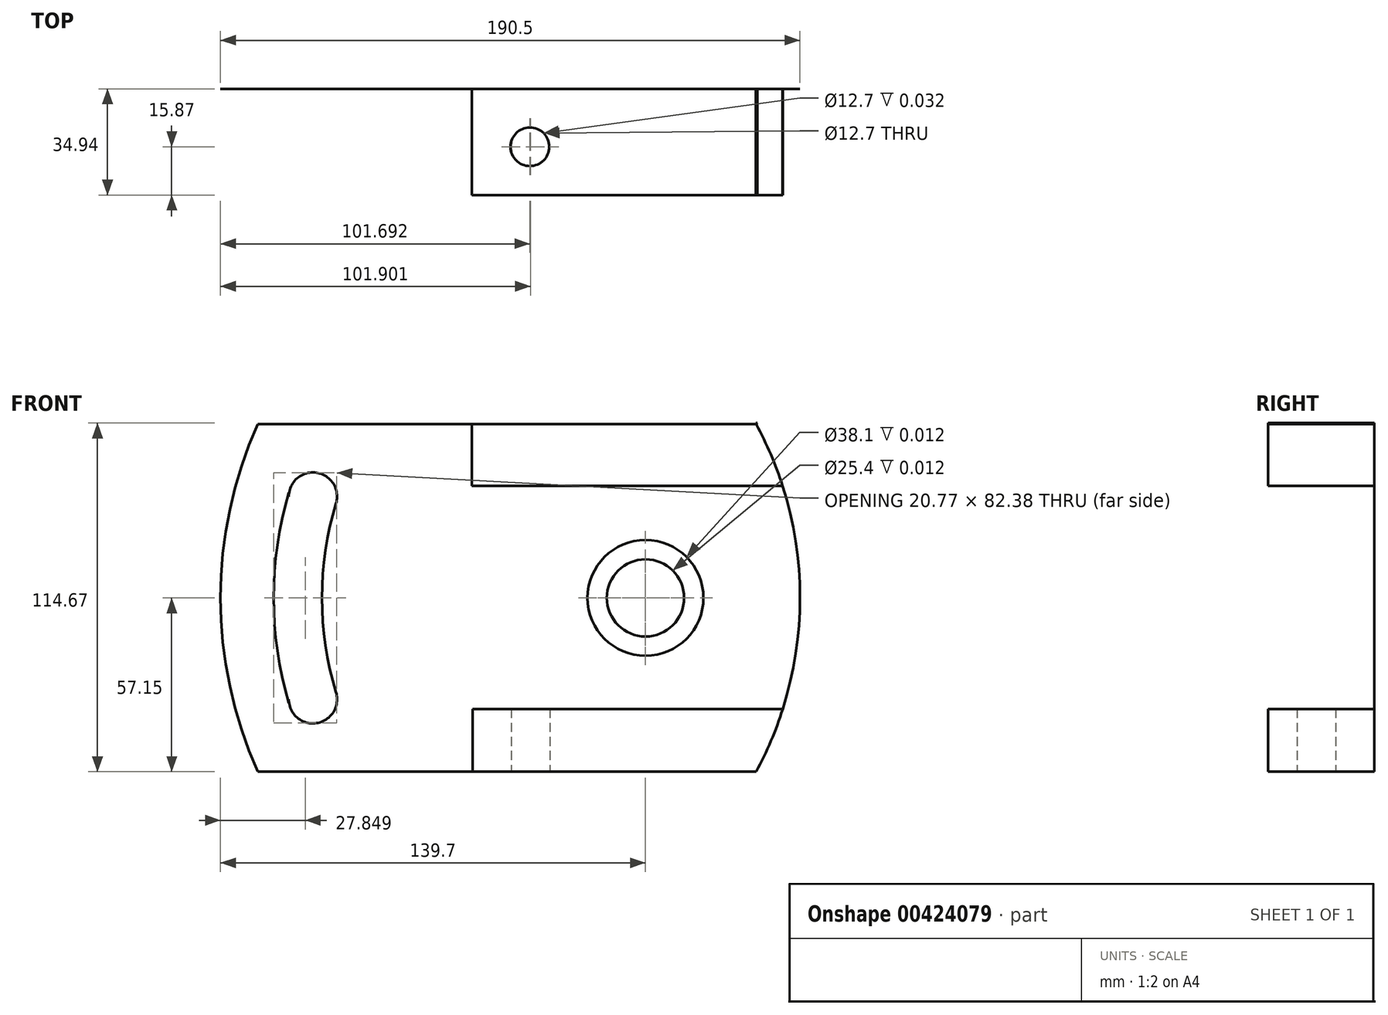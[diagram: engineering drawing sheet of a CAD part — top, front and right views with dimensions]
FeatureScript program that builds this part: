
annotation { "Feature Type Name" : "Feature", "Feature Type Description" : "" }
export const myFeature = defineFeature(function(context is Context, id is Id, definition is map)
    precondition{}
    {
        {
            var Q0;
            Q0=qCreatedBy(makeId("Front.planeOp"),FACE);
            var sketch = newSketch(context, id + "F0", { "sketchPlane" : qUnion([Q0])});
            skLineSegment(sketch, "E0.bottom", {"start": v(0, 0) * mm, "end": v(190.5, 0) * mm});
            skLineSegment(sketch, "E0.top", {"start": v(0, 114.3) * mm, "end": v(190.5, 114.3) * mm});
            skLineSegment(sketch, "E0.left", {"start": v(0, 0) * mm, "end": v(0, 114.3) * mm});
            skLineSegment(sketch, "E0.right", {"start": v(190.5, 0) * mm, "end": v(190.5, 114.3) * mm});
            skSolve(sketch);
        }
        {
            var Q0;
            Q0=makeQuery(id+"F0.imprint","IMPRINT",FACE,{"disambiguationData":[TD([[makeQuery(id+"F0.imprint","IMPRINT",EDGE,{"derivedFrom":sQuery(id+"F0.wireOp",EDGE,"E0.bottom")}),1.0]])]});
            extrude(context, id + "F1", {"entities" : qUnion([Q0]), "oppositeDirection" : true, "depth" : 5 / 203.2 * mm});
        }
        {
            var Q0;
            Q0=makeQuery(id+"F1.opExtrude","CAP_FACE",FACE,{"disambiguationData":[OSD([sQuery(id+"F0.wireOp",EDGE,"E0.bottom"),sQuery(id+"F0.wireOp",EDGE,"E0.top"),sQuery(id+"F0.wireOp",EDGE,"E0.left"),sQuery(id+"F0.wireOp",EDGE,"E0.right")])],"isStart":true});
            var sketch = newSketch(context, id + "F2", { "sketchPlane" : qUnion([Q0])});
            skLineSegment(sketch, "E1", {"start": v(0, 57.15) * mm, "end": v(139.7, 57.15) * mm});
            skCircle(sketch, "E2", {"center": v(139.7, 57.15) * mm, "radius": 19.05 * mm});
            skCircle(sketch, "E3", {"center": v(139.7, 57.15) * mm, "radius": 12.7 * mm});
            skCircle(sketch, "E4", {"center": v(139.7, 57.15) * mm, "radius": 114.3 * mm});
            skCircle(sketch, "E5", {"center": v(139.7, 57.15) * mm, "radius": 139.7 * mm});
            skCircle(sketch, "E6", {"center": v(69.85, 57.15) * mm, "radius": 120.65 * mm});
            skLineSegment(sketch, "E7.bottom", {"start": v(22.43, 98.42) * mm, "end": v(38.3, 98.42) * mm});
            skLineSegment(sketch, "E7.top", {"start": v(22.43, 15.87) * mm, "end": v(38.3, 15.87) * mm});
            skLineSegment(sketch, "E7.left", {"start": v(22.43, 98.43) * mm, "end": v(22.43, 15.88) * mm});
            skLineSegment(sketch, "E7.right", {"start": v(38.3, 98.43) * mm, "end": v(38.3, 15.88) * mm});
            skCircle(sketch, "E8", {"center": v(30.37, 90.49) * mm, "radius": 7.94 * mm});
            skCircle(sketch, "E9", {"center": v(30.37, 23.81) * mm, "radius": 7.94 * mm});
            skPoint(sketch, "E9.centerSnap0", {"position": v(30.37, 15.88) * mm});
            skCircle(sketch, "E10", {"center": v(139.7, 57.15) * mm, "radius": 106.36 * mm});
            skCircle(sketch, "E11", {"center": v(139.7, 57.15) * mm, "radius": 122.24 * mm});
            skSolve(sketch);
        }
        {
            var Q0;
            Q0=makeQuery(id+"F2.imprint","IMPRINT",FACE,{"disambiguationData":[TD([[makeQuery(id+"F2.imprint","IMPRINT",EDGE,{"derivedFrom":sQuery(id+"F2.wireOp",EDGE,"E2")}),-1.0]])]});
            var sketch = newSketch(context, id + "F3", { "sketchPlane" : qUnion([Q0])});
            skLineSegment(sketch, "E12.bottom", {"start": v(190.6, 114.67) * mm, "end": v(82.64, 114.67) * mm});
            skLineSegment(sketch, "E12.top", {"start": v(190.6, 94.03) * mm, "end": v(82.64, 94.03) * mm});
            skLineSegment(sketch, "E12.left", {"start": v(190.6, 114.67) * mm, "end": v(190.6, 94.03) * mm});
            skLineSegment(sketch, "E12.right", {"start": v(82.64, 114.67) * mm, "end": v(82.64, 94.03) * mm});
            skLineSegment(sketch, "E13.bottom", {"start": v(190.8, 0) * mm, "end": v(82.85, 0) * mm});
            skLineSegment(sketch, "E13.top", {"start": v(190.8, 20.64) * mm, "end": v(82.85, 20.64) * mm});
            skLineSegment(sketch, "E13.left", {"start": v(190.8, 0) * mm, "end": v(190.8, 20.64) * mm});
            skLineSegment(sketch, "E13.right", {"start": v(82.85, 0) * mm, "end": v(82.85, 20.64) * mm});
            skSolve(sketch);
        }
        {
            var Q0;
            {var subQ0=sQuery(id+"F2.wireOp",EDGE,"E6");var subQ1=makeQuery(id+"F1.opExtrude","CAP_EDGE",EDGE,{"disambiguationData":[OSD([sQuery(id+"F0.wireOp",EDGE,"E0.top")])],"isStart":true});var subQ2=makeQuery(id+"F2.imprint","INTERSECT",VERTEX,{"derivedFrom":[subQ1,subQ0]});Q0=makeQuery(id+"F2.imprint","IMPRINT",FACE,{"disambiguationData":[TD([[makeQuery(id+"F2.imprint","IMPRINT",EDGE,{"disambiguationData":[TD([[subQ2,1.0]])],"derivedFrom":subQ0}),-1.0]])]});}
            var Q1;
            {var subQ0=sQuery(id+"F2.wireOp",EDGE,"E6");var subQ1=makeQuery(id+"F1.opExtrude","CAP_EDGE",EDGE,{"disambiguationData":[OSD([sQuery(id+"F0.wireOp",EDGE,"E0.right")])],"isStart":true});var subQ2=makeQuery(id+"F2.imprint","INTERSECT",VERTEX,{"derivedFrom":[subQ1,subQ0]});Q1=makeQuery(id+"F2.imprint","IMPRINT",FACE,{"disambiguationData":[TD([[makeQuery(id+"F2.imprint","IMPRINT",EDGE,{"disambiguationData":[TD([[subQ2,1.0]])],"derivedFrom":subQ0}),-1.0]])]});}
            var Q2;
            {var subQ1=makeQuery(id+"F1.opExtrude","CAP_EDGE",EDGE,{"disambiguationData":[OSD([sQuery(id+"F0.wireOp",EDGE,"E0.left")])],"isStart":true});var subQ3=makeQuery(id+"F1.opExtrude","CAP_EDGE",EDGE,{"disambiguationData":[OSD([sQuery(id+"F0.wireOp",EDGE,"E0.top")])],"isStart":true});var subQ5=makeQuery(id+"F2.imprint","INTERSECT",VERTEX,{"derivedFrom":[subQ3,subQ1]});Q2=makeQuery(id+"F2.imprint","IMPRINT",FACE,{"disambiguationData":[TD([[makeQuery(id+"F2.imprint","IMPRINT",EDGE,{"disambiguationData":[TD([[subQ5,-1.0]])],"derivedFrom":subQ3}),-1.0]])]});}
            var Q3;
            {var subQ1=makeQuery(id+"F1.opExtrude","CAP_EDGE",EDGE,{"disambiguationData":[OSD([sQuery(id+"F0.wireOp",EDGE,"E0.left")])],"isStart":true});var subQ3=makeQuery(id+"F1.opExtrude","CAP_EDGE",EDGE,{"disambiguationData":[OSD([sQuery(id+"F0.wireOp",EDGE,"E0.bottom")])],"isStart":true});var subQ5=makeQuery(id+"F2.imprint","INTERSECT",VERTEX,{"derivedFrom":[subQ3,subQ1]});Q3=makeQuery(id+"F2.imprint","IMPRINT",FACE,{"disambiguationData":[TD([[makeQuery(id+"F2.imprint","IMPRINT",EDGE,{"disambiguationData":[TD([[subQ5,-1.0]])],"derivedFrom":subQ3}),1.0]])]});}
            extrude(context, id + "F4", {"entities" : qUnion([Q0, Q1, Q2, Q3]), "operationType" : NewBodyOperationType.REMOVE, "oppositeDirection" : true, "depth" : 25.4 * mm});
        }
        {
            var Q0;
            Q0 = qSketchRegion(id + "F2", true);
            extrude(context, id + "F5", {"entities" : qUnion([Q0]), "operationType" : NewBodyOperationType.REMOVE, "oppositeDirection" : true, "depth" : 25.4 * mm});
        }
        {
            var Q0;
            Q0=makeQuery(id+"F2.imprint","IMPRINT",FACE,{"disambiguationData":[TD([[makeQuery(id+"F2.imprint","IMPRINT",EDGE,{"derivedFrom":sQuery(id+"F2.wireOp",EDGE,"E2")}),-1.0]])]});
            var sketch = newSketch(context, id + "F6", { "sketchPlane" : qUnion([Q0])});
            skLineSegment(sketch, "E14.bottom", {"start": v(0, 0) * mm, "end": v(41.97, 0) * mm});
            skLineSegment(sketch, "E14.top", {"start": v(0, 114.3) * mm, "end": v(41.97, 114.3) * mm});
            skLineSegment(sketch, "E14.left", {"start": v(0, 0) * mm, "end": v(0, 114.3) * mm});
            skLineSegment(sketch, "E14.right", {"start": v(41.97, 0) * mm, "end": v(41.97, 114.3) * mm});
            skArc(sketch, "E15", {"start": v(12.27, 114.3) * mm, "mid": v(0.69, 57.03) * mm, "end": v(13.37, 0) * mm});
            skSolve(sketch);
        }
        {
            var Q0;
            {var subQ0=sQuery(id+"F2.wireOp",EDGE,"E7.left");var subQ1=sQuery(id+"F2.wireOp",EDGE,"E7.bottom");var subQ2=makeQuery(id+"F2.imprint","INTERSECT",VERTEX,{"derivedFrom":[subQ1,subQ0]});Q0=makeQuery(id+"F2.imprint","IMPRINT",FACE,{"disambiguationData":[TD([[makeQuery(id+"F2.imprint","IMPRINT",EDGE,{"disambiguationData":[TD([[subQ2,-1.0]])],"derivedFrom":subQ1}),1.0]])]});}
            var Q1;
            {var subQ0=sQuery(id+"F2.wireOp",EDGE,"E7.left");var subQ1=sQuery(id+"F2.wireOp",EDGE,"E7.top");var subQ2=makeQuery(id+"F2.imprint","INTERSECT",VERTEX,{"derivedFrom":[subQ1,subQ0]});Q1=makeQuery(id+"F2.imprint","IMPRINT",FACE,{"disambiguationData":[TD([[makeQuery(id+"F2.imprint","IMPRINT",EDGE,{"disambiguationData":[TD([[subQ2,-1.0]])],"derivedFrom":subQ1}),-1.0]])]});}
            extrude(context, id + "F7", {"entities" : qUnion([Q0, Q1]), "operationType" : NewBodyOperationType.ADD, "oppositeDirection" : true, "depth" : 5 / 203.2 * mm});
        }
        {
            var Q0;
            {var subQ0=sQuery(id+"F2.wireOp",EDGE,"E6");var subQ1=makeQuery(id+"F1.opExtrude","CAP_EDGE",EDGE,{"disambiguationData":[OSD([sQuery(id+"F0.wireOp",EDGE,"E0.top")])],"isStart":true});var subQ2=makeQuery(id+"F2.imprint","INTERSECT",VERTEX,{"derivedFrom":[subQ1,subQ0]});Q0=makeQuery(id+"F2.imprint","IMPRINT",FACE,{"disambiguationData":[TD([[makeQuery(id+"F2.imprint","IMPRINT",EDGE,{"disambiguationData":[TD([[subQ2,1.0]])],"derivedFrom":subQ0}),-1.0]])]});}
            var Q1;
            {var subQ0=sQuery(id+"F2.wireOp",EDGE,"E6");var subQ1=makeQuery(id+"F1.opExtrude","CAP_EDGE",EDGE,{"disambiguationData":[OSD([sQuery(id+"F0.wireOp",EDGE,"E0.right")])],"isStart":true});var subQ2=makeQuery(id+"F2.imprint","INTERSECT",VERTEX,{"derivedFrom":[subQ1,subQ0]});Q1=makeQuery(id+"F2.imprint","IMPRINT",FACE,{"disambiguationData":[TD([[makeQuery(id+"F2.imprint","IMPRINT",EDGE,{"disambiguationData":[TD([[subQ2,1.0]])],"derivedFrom":subQ0}),-1.0]])]});}
            extrude(context, id + "F8", {"entities" : qUnion([Q0, Q1]), "operationType" : NewBodyOperationType.REMOVE, "oppositeDirection" : true, "depth" : 25.4 * mm});
        }
        {
            var Q0;
            {var subQ0=sQuery(id+"F2.wireOp",EDGE,"E8");var subQ1=sQuery(id+"F2.wireOp",EDGE,"E4");var subQ2=makeQuery(id+"F2.imprint","INTERSECT",VERTEX,{"disambiguationData":[OD(0.0)],"derivedFrom":[subQ1,subQ0]});Q0=makeQuery(id+"F2.imprint","IMPRINT",FACE,{"disambiguationData":[TD([[makeQuery(id+"F2.imprint","IMPRINT",EDGE,{"disambiguationData":[TD([[subQ2,-1.0]])],"derivedFrom":subQ1}),1.0]])]});}
            var Q1;
            {var subQ0=sQuery(id+"F2.wireOp",EDGE,"E8");var subQ4=sQuery(id+"F2.wireOp",EDGE,"E4");var subQ5=makeQuery(id+"F2.imprint","INTERSECT",VERTEX,{"disambiguationData":[OD(0.0)],"derivedFrom":[subQ4,subQ0]});Q1=makeQuery(id+"F2.imprint","IMPRINT",FACE,{"disambiguationData":[TD([[makeQuery(id+"F2.imprint","IMPRINT",EDGE,{"disambiguationData":[TD([[subQ5,-1.0]])],"derivedFrom":subQ4}),-1.0]])]});}
            var Q2;
            {var subQ0=sQuery(id+"F2.wireOp",EDGE,"E7.left");var subQ1=sQuery(id+"F2.wireOp",EDGE,"E1");var subQ2=makeQuery(id+"F2.imprint","INTERSECT",VERTEX,{"derivedFrom":[subQ1,subQ0]});Q2=makeQuery(id+"F2.imprint","IMPRINT",FACE,{"disambiguationData":[TD([[makeQuery(id+"F2.imprint","IMPRINT",EDGE,{"disambiguationData":[TD([[subQ2,-1.0]])],"derivedFrom":subQ1}),1.0]])]});}
            var Q3;
            {var subQ0=sQuery(id+"F2.wireOp",EDGE,"E11");var subQ1=sQuery(id+"F2.wireOp",EDGE,"E1");var subQ2=makeQuery(id+"F2.imprint","INTERSECT",VERTEX,{"derivedFrom":[subQ1,subQ0]});Q3=makeQuery(id+"F2.imprint","IMPRINT",FACE,{"disambiguationData":[TD([[makeQuery(id+"F2.imprint","IMPRINT",EDGE,{"disambiguationData":[TD([[subQ2,-1.0]])],"derivedFrom":subQ1}),1.0]])]});}
            var Q4;
            {var subQ0=sQuery(id+"F2.wireOp",EDGE,"E4");var subQ1=sQuery(id+"F2.wireOp",EDGE,"E1");var subQ2=makeQuery(id+"F2.imprint","INTERSECT",VERTEX,{"derivedFrom":[subQ1,subQ0]});Q4=makeQuery(id+"F2.imprint","IMPRINT",FACE,{"disambiguationData":[TD([[makeQuery(id+"F2.imprint","IMPRINT",EDGE,{"disambiguationData":[TD([[subQ2,-1.0]])],"derivedFrom":subQ1}),1.0]])]});}
            var Q5;
            {var subQ0=sQuery(id+"F2.wireOp",EDGE,"E4");var subQ1=sQuery(id+"F2.wireOp",EDGE,"E1");var subQ2=makeQuery(id+"F2.imprint","INTERSECT",VERTEX,{"derivedFrom":[subQ1,subQ0]});Q5=makeQuery(id+"F2.imprint","IMPRINT",FACE,{"disambiguationData":[TD([[makeQuery(id+"F2.imprint","IMPRINT",EDGE,{"disambiguationData":[TD([[subQ2,-1.0]])],"derivedFrom":subQ1}),-1.0]])]});}
            var Q6;
            {var subQ0=sQuery(id+"F2.wireOp",EDGE,"E7.left");var subQ1=sQuery(id+"F2.wireOp",EDGE,"E1");var subQ2=makeQuery(id+"F2.imprint","INTERSECT",VERTEX,{"derivedFrom":[subQ1,subQ0]});Q6=makeQuery(id+"F2.imprint","IMPRINT",FACE,{"disambiguationData":[TD([[makeQuery(id+"F2.imprint","IMPRINT",EDGE,{"disambiguationData":[TD([[subQ2,-1.0]])],"derivedFrom":subQ1}),-1.0]])]});}
            var Q7;
            {var subQ0=sQuery(id+"F2.wireOp",EDGE,"E11");var subQ1=sQuery(id+"F2.wireOp",EDGE,"E1");var subQ2=makeQuery(id+"F2.imprint","INTERSECT",VERTEX,{"derivedFrom":[subQ1,subQ0]});Q7=makeQuery(id+"F2.imprint","IMPRINT",FACE,{"disambiguationData":[TD([[makeQuery(id+"F2.imprint","IMPRINT",EDGE,{"disambiguationData":[TD([[subQ2,-1.0]])],"derivedFrom":subQ1}),-1.0]])]});}
            var Q8;
            {var subQ0=sQuery(id+"F2.wireOp",EDGE,"E9");var subQ4=sQuery(id+"F2.wireOp",EDGE,"E4");var subQ5=makeQuery(id+"F2.imprint","INTERSECT",VERTEX,{"disambiguationData":[OD(0.0)],"derivedFrom":[subQ4,subQ0]});Q8=makeQuery(id+"F2.imprint","IMPRINT",FACE,{"disambiguationData":[TD([[makeQuery(id+"F2.imprint","IMPRINT",EDGE,{"disambiguationData":[TD([[subQ5,-1.0]])],"derivedFrom":subQ4}),-1.0]])]});}
            var Q9;
            {var subQ0=sQuery(id+"F2.wireOp",EDGE,"E9");var subQ1=sQuery(id+"F2.wireOp",EDGE,"E4");var subQ2=makeQuery(id+"F2.imprint","INTERSECT",VERTEX,{"disambiguationData":[OD(0.0)],"derivedFrom":[subQ1,subQ0]});Q9=makeQuery(id+"F2.imprint","IMPRINT",FACE,{"disambiguationData":[TD([[makeQuery(id+"F2.imprint","IMPRINT",EDGE,{"disambiguationData":[TD([[subQ2,-1.0]])],"derivedFrom":subQ1}),1.0]])]});}
            extrude(context, id + "F9", {"entities" : qUnion([Q0, Q1, Q2, Q3, Q4, Q5, Q6, Q7, Q8, Q9]), "operationType" : NewBodyOperationType.REMOVE, "oppositeDirection" : true, "depth" : 25.4 * mm});
        }
        {
            var Q0;
            Q0 = qSketchRegion(id + "F3", true);
            extrude(context, id + "F10", {"entities" : qUnion([Q0]), "operationType" : NewBodyOperationType.ADD, "depth" : 34.92 * mm});
        }
        {
            var Q0;
            {var subQ0=sQuery(id+"F0.wireOp",EDGE,"E0.top");var subQ1=sQuery(id+"F0.wireOp",EDGE,"E0.bottom");Q0=makeQuery(id+"F7.boolean.opBoolean","MERGE",FACE,{"derivedFrom":[makeQuery(id+"F1.opExtrude","CAP_FACE",FACE,{"disambiguationData":[OSD([subQ1,subQ0,sQuery(id+"F0.wireOp",EDGE,"E0.left"),sQuery(id+"F0.wireOp",EDGE,"E0.right")])],"isStart":false}),makeQuery(id+"F7.opExtrude","CAP_FACE",FACE,{"disambiguationData":[OSD([subQ1,subQ0,sQuery(id+"F2.wireOp",EDGE,"E5"),sQuery(id+"F2.wireOp",EDGE,"E7.bottom"),sQuery(id+"F2.wireOp",EDGE,"E7.top"),sQuery(id+"F2.wireOp",EDGE,"E7.left"),sQuery(id+"F2.wireOp",EDGE,"E11")])],"isStart":false})]});}
            var sketch = newSketch(context, id + "F11", { "sketchPlane" : qUnion([Q0])});
            skLineSegment(sketch, "E16", {"start": v(-176.1, 114.3) * mm, "end": v(-261.02, 202.77) * mm});
            skLineSegment(sketch, "E17", {"start": v(-261.02, 202.77) * mm, "end": v(-261.02, -36.6) * mm});
            skLineSegment(sketch, "E18", {"start": v(-261.02, -36.6) * mm, "end": v(-176.1, 0) * mm});
            skCircle(sketch, "E19", {"center": v(-69.85, 57.15) * mm, "radius": 120.65 * mm});
            skSolve(sketch);
        }
        {
            var Q0;
            Q0=makeQuery(id+"F11.imprint","IMPRINT",FACE,{"disambiguationData":[TD([[makeQuery(id+"F11.imprint","IMPRINT",EDGE,{"disambiguationData":[OD(1.0)],"derivedFrom":sQuery(id+"F11.wireOp",EDGE,"E19")}),1.0]])]});
            var Q1;
            {var subQ1=sQuery(id+"F2.wireOp",EDGE,"E11");var subQ2=sQuery(id+"F2.wireOp",EDGE,"E7.left");var subQ3=sQuery(id+"F0.wireOp",EDGE,"E0.top");var subQ4=sQuery(id+"F0.wireOp",EDGE,"E0.bottom");var subQ5=makeQuery(id+"F7.boolean.opBoolean","MERGE",FACE,{"derivedFrom":[makeQuery(id+"F1.opExtrude","CAP_FACE",FACE,{"disambiguationData":[OSD([subQ4,subQ3,sQuery(id+"F0.wireOp",EDGE,"E0.left"),sQuery(id+"F0.wireOp",EDGE,"E0.right")])],"isStart":false}),makeQuery(id+"F7.opExtrude","CAP_FACE",FACE,{"disambiguationData":[OSD([subQ4,subQ3,sQuery(id+"F2.wireOp",EDGE,"E5"),sQuery(id+"F2.wireOp",EDGE,"E7.bottom"),sQuery(id+"F2.wireOp",EDGE,"E7.top"),subQ2,subQ1])],"isStart":false})]});var subQ6=sQuery(id+"F2.wireOp",EDGE,"E8");Q1=makeQuery(id+"F11.imprint","IMPRINT",FACE,{"disambiguationData":[TD([[makeQuery(id+"F11.imprint","IMPRINT",EDGE,{"derivedFrom":makeQuery(id+"F9.boolean.opBoolean","INTERSECT",EDGE,{"derivedFrom":[subQ5,makeQuery(id+"F9.opExtrude","SWEPT_FACE",FACE,{"disambiguationData":[OSD([subQ6])]})]})}),-1.0]])]});}
            var Q2;
            Q2=makeQuery(id+"F11.imprint","IMPRINT",FACE,{"disambiguationData":[TD([[makeQuery(id+"F11.imprint","IMPRINT",EDGE,{"derivedFrom":sQuery(id+"F11.wireOp",EDGE,"E16")}),1.0]])]});
            extrude(context, id + "F12", {"entities" : qUnion([Q0, Q1, Q2]), "operationType" : NewBodyOperationType.REMOVE, "oppositeDirection" : true, "depth" : 86.36 * mm});
        }
        {
            var Q0;
            {var subQ0=sQuery(id+"F0.wireOp",EDGE,"E0.top");Q0=makeQuery(id+"F12.boolean.opBoolean","MERGE",FACE,{"derivedFrom":[makeQuery(id+"F7.boolean.opBoolean","MERGE",FACE,{"derivedFrom":[makeQuery(id+"F1.opExtrude","SWEPT_FACE",FACE,{"disambiguationData":[OSD([subQ0])]}),makeQuery(id+"F7.opExtrude","SWEPT_FACE",FACE,{"disambiguationData":[OSD([subQ0])]})]}),makeQuery(id+"F12.opExtrude","SWEPT_FACE",FACE,{"disambiguationData":[OSD([subQ0])]})]});}
            var sketch = newSketch(context, id + "F13", { "sketchPlane" : qUnion([Q0])});
            skLineSegment(sketch, "E20.bottom", {"start": v(82.64, 0) * mm, "end": v(101.7, 0) * mm});
            skLineSegment(sketch, "E20.top", {"start": v(82.64, -19.05) * mm, "end": v(101.7, -19.05) * mm});
            skLineSegment(sketch, "E20.left", {"start": v(82.64, 0) * mm, "end": v(82.64, -19.05) * mm});
            skLineSegment(sketch, "E20.right", {"start": v(101.7, 0) * mm, "end": v(101.7, -19.05) * mm});
            skCircle(sketch, "E21", {"center": v(101.7, -19.05) * mm, "radius": 6.35 * mm});
            skSolve(sketch);
        }
        {
            var Q0;
            {var subQ0=sQuery(id+"F0.wireOp",EDGE,"E0.bottom");Q0=makeQuery(id+"F10.boolean.opBoolean","MERGE",FACE,{"derivedFrom":[makeQuery(id+"F7.boolean.opBoolean","MERGE",FACE,{"derivedFrom":[makeQuery(id+"F1.opExtrude","SWEPT_FACE",FACE,{"disambiguationData":[OSD([subQ0])]}),makeQuery(id+"F7.opExtrude","SWEPT_FACE",FACE,{"disambiguationData":[OSD([subQ0])]})]}),makeQuery(id+"F10.opExtrude","SWEPT_FACE",FACE,{"disambiguationData":[OSD([sQuery(id+"F3.wireOp",EDGE,"E13.bottom")])]})]});}
            var sketch = newSketch(context, id + "F14", { "sketchPlane" : qUnion([Q0])});
            skLineSegment(sketch, "E22.bottom", {"start": v(82.85, 0) * mm, "end": v(101.9, 0) * mm});
            skLineSegment(sketch, "E22.top", {"start": v(82.85, 19.05) * mm, "end": v(101.9, 19.05) * mm});
            skLineSegment(sketch, "E22.left", {"start": v(82.85, 0) * mm, "end": v(82.85, 19.05) * mm});
            skLineSegment(sketch, "E22.right", {"start": v(101.9, 0) * mm, "end": v(101.9, 19.05) * mm});
            skCircle(sketch, "E23", {"center": v(101.9, 19.05) * mm, "radius": 6.35 * mm});
            skSolve(sketch);
        }
        {
            var Q0;
            {var subQ0=sQuery(id+"F13.wireOp",EDGE,"E20.right");var subQ1=sQuery(id+"F13.wireOp",EDGE,"E20.top");var subQ2=makeQuery(id+"F13.imprint","INTERSECT",VERTEX,{"derivedFrom":[subQ1,subQ0]});Q0=makeQuery(id+"F13.imprint","IMPRINT",FACE,{"disambiguationData":[TD([[makeQuery(id+"F13.imprint","IMPRINT",EDGE,{"disambiguationData":[TD([[subQ2,1.0]])],"derivedFrom":subQ1}),-1.0]])]});}
            var Q1;
            {var subQ0=sQuery(id+"F13.wireOp",EDGE,"E20.right");var subQ1=sQuery(id+"F13.wireOp",EDGE,"E20.top");var subQ2=makeQuery(id+"F13.imprint","INTERSECT",VERTEX,{"derivedFrom":[subQ1,subQ0]});Q1=makeQuery(id+"F13.imprint","IMPRINT",FACE,{"disambiguationData":[TD([[makeQuery(id+"F13.imprint","IMPRINT",EDGE,{"disambiguationData":[TD([[subQ2,1.0]])],"derivedFrom":subQ1}),1.0]])]});}
            extrude(context, id + "F15", {"entities" : qUnion([Q0, Q1]), "operationType" : NewBodyOperationType.REMOVE, "oppositeDirection" : true, "depth" : 13 / 406.4 * mm});
        }
        {
            var Q0;
            {var subQ0=sQuery(id+"F14.wireOp",EDGE,"E22.right");var subQ1=sQuery(id+"F14.wireOp",EDGE,"E22.top");var subQ2=makeQuery(id+"F14.imprint","INTERSECT",VERTEX,{"derivedFrom":[subQ1,subQ0]});Q0=makeQuery(id+"F14.imprint","IMPRINT",FACE,{"disambiguationData":[TD([[makeQuery(id+"F14.imprint","IMPRINT",EDGE,{"disambiguationData":[TD([[subQ2,1.0]])],"derivedFrom":subQ1}),1.0]])]});}
            var Q1;
            {var subQ0=sQuery(id+"F14.wireOp",EDGE,"E22.right");var subQ1=sQuery(id+"F14.wireOp",EDGE,"E22.top");var subQ2=makeQuery(id+"F14.imprint","INTERSECT",VERTEX,{"derivedFrom":[subQ1,subQ0]});Q1=makeQuery(id+"F14.imprint","IMPRINT",FACE,{"disambiguationData":[TD([[makeQuery(id+"F14.imprint","IMPRINT",EDGE,{"disambiguationData":[TD([[subQ2,1.0]])],"derivedFrom":subQ1}),-1.0]])]});}
            extrude(context, id + "F16", {"entities" : qUnion([Q0, Q1]), "operationType" : NewBodyOperationType.REMOVE, "oppositeDirection" : true, "depth" : 25.4 * mm});
        }
        {
            var Q0;
            Q0=makeQuery(id+"F6.imprint","IMPRINT",FACE,{"disambiguationData":[TD([[makeQuery(id+"F6.imprint","IMPRINT",EDGE,{"derivedFrom":makeQuery(id+"F2.imprint","IMPRINT",EDGE,{"derivedFrom":sQuery(id+"F2.wireOp",EDGE,"E2")})}),1.0]])]});
            extrude(context, id + "F17", {"entities" : qUnion([Q0]), "operationType" : NewBodyOperationType.REMOVE, "oppositeDirection" : true, "depth" : 5 / 406.4 * mm});
        }
        {
            var Q0;
            Q0=makeQuery(id+"F2.imprint","IMPRINT",FACE,{"disambiguationData":[TD([[makeQuery(id+"F2.imprint","IMPRINT",EDGE,{"derivedFrom":sQuery(id+"F2.wireOp",EDGE,"E3")}),1.0]])]});
            extrude(context, id + "F18", {"entities" : qUnion([Q0]), "operationType" : NewBodyOperationType.REMOVE, "oppositeDirection" : true, "depth" : 5 / 203.2 * mm});
        }
    });
